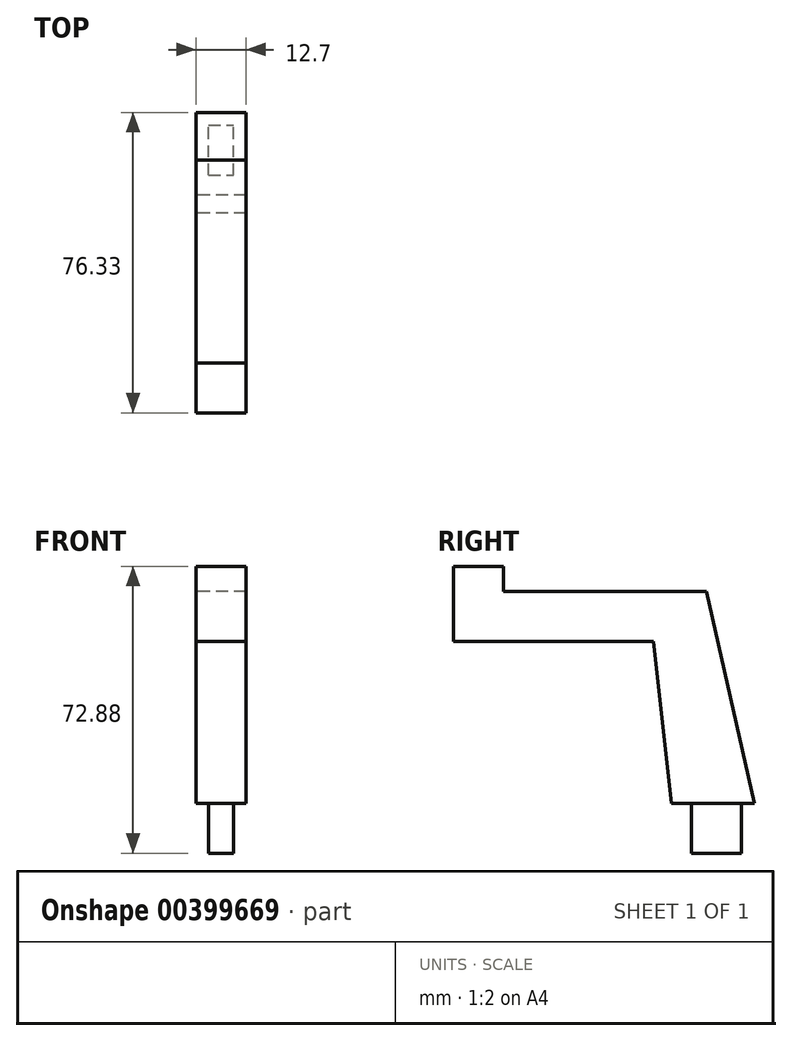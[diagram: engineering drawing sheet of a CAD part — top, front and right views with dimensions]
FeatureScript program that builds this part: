
annotation { "Feature Type Name" : "Feature", "Feature Type Description" : "" }
export const myFeature = defineFeature(function(context is Context, id is Id, definition is map)
    precondition{}
    {
        {
            var Q0;
            Q0=qCreatedBy(makeId("Right.planeOp"),FACE);
            var sketch = newSketch(context, id + "F0", { "sketchPlane" : qUnion([Q0])});
            skLineSegment(sketch, "E0", {"start": v(61.75, -154.7) * mm, "end": v(23.78, 14.53) * mm});
            skLineSegment(sketch, "E1", {"start": v(11.7, 68.36) * mm, "end": v(-39.85, 68.36) * mm});
            skLineSegment(sketch, "E2", {"start": v(-39.85, 68.36) * mm, "end": v(-39.85, 74.71) * mm});
            skLineSegment(sketch, "E3", {"start": v(-39.85, 74.71) * mm, "end": v(-52.55, 74.71) * mm});
            skLineSegment(sketch, "E4", {"start": v(-52.55, 74.71) * mm, "end": v(-52.55, 55.66) * mm});
            skLineSegment(sketch, "E5", {"start": v(-52.55, 55.66) * mm, "end": v(-1.75, 55.66) * mm});
            skLineSegment(sketch, "E6", {"start": v(2.71, 14.53) * mm, "end": v(21.1, -154.73) * mm});
            skLineSegment(sketch, "E7", {"start": v(21.1, -154.73) * mm, "end": v(61.75, -154.7) * mm});
            skCircle(sketch, "E8", {"center": v(18.75, -21.39) * mm, "radius": 6.48 * mm});
            skCircle(sketch, "E9", {"center": v(33.52, -110.27) * mm, "radius": 6.48 * mm});
            skLineSegment(sketch, "E10", {"start": v(23.78, 14.53) * mm, "end": v(2.71, 14.53) * mm});
            skLineSegment(sketch, "E11", {"start": v(23.78, 14.53) * mm, "end": v(11.7, 68.36) * mm});
            skLineSegment(sketch, "E12", {"start": v(-1.75, 55.66) * mm, "end": v(2.71, 14.53) * mm});
            skSolve(sketch);
        }
        {
            var Q0;
            Q0=makeQuery(id+"F0.imprint","IMPRINT",FACE,{"disambiguationData":[TD([[makeQuery(id+"F0.imprint","IMPRINT",EDGE,{"derivedFrom":sQuery(id+"F0.wireOp",EDGE,"E1")}),1.0]])]});
            extrude(context, id + "F1", {"entities" : qUnion([Q0]), "endBound" : BoundingType.SYMMETRIC, "depth" : 12.7 * mm});
        }
        {
            var Q0;
            Q0=makeQuery(id+"F1.opExtrude","SWEPT_FACE",FACE,{"disambiguationData":[OSD([sQuery(id+"F0.wireOp",EDGE,"E10")])]});
            var sketch = newSketch(context, id + "F2", { "sketchPlane" : qUnion([Q0])});
            skLineSegment(sketch, "E13.bottom", {"start": v(-3.18, -7.8) * mm, "end": v(3.17, -7.8) * mm});
            skLineSegment(sketch, "E13.top", {"start": v(-3.17, -20.5) * mm, "end": v(3.18, -20.5) * mm});
            skLineSegment(sketch, "E13.left", {"start": v(-3.18, -7.8) * mm, "end": v(-3.17, -20.5) * mm});
            skLineSegment(sketch, "E13.right", {"start": v(3.17, -7.8) * mm, "end": v(3.18, -20.5) * mm});
            skSolve(sketch);
        }
        {
            var Q0;
            Q0=makeQuery(id+"F2.imprint","IMPRINT",FACE,{"disambiguationData":[TD([[makeQuery(id+"F2.imprint","IMPRINT",EDGE,{"derivedFrom":sQuery(id+"F2.wireOp",EDGE,"E13.bottom")}),-1.0]])]});
            extrude(context, id + "F3", {"entities" : qUnion([Q0]), "operationType" : NewBodyOperationType.ADD, "depth" : 12.7 * mm});
        }
    });
